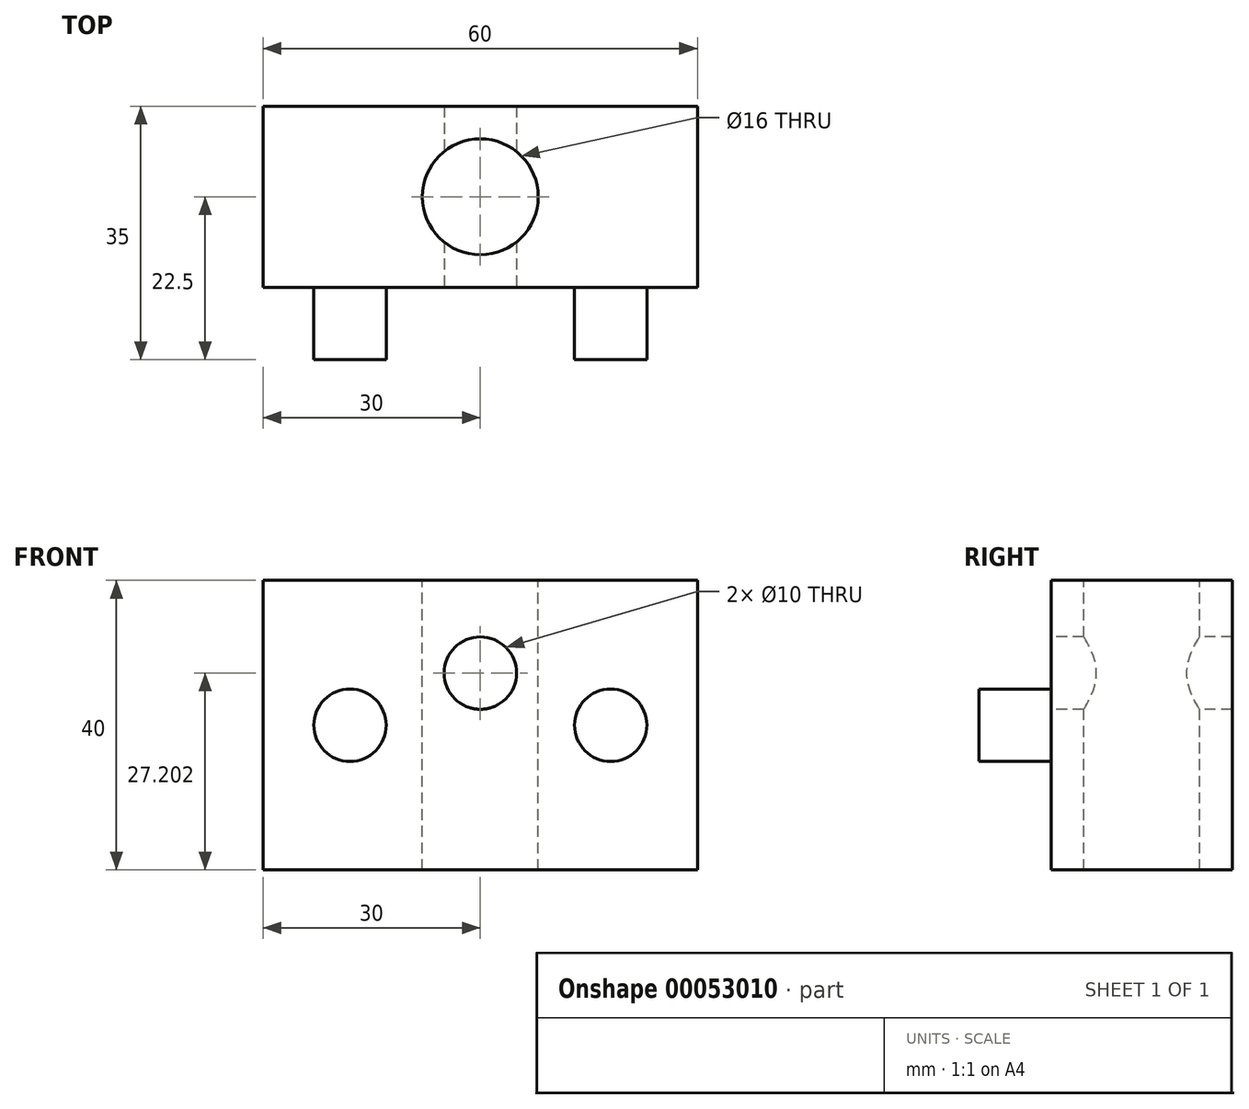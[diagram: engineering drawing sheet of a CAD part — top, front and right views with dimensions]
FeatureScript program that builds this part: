
annotation { "Feature Type Name" : "Feature", "Feature Type Description" : "" }
export const myFeature = defineFeature(function(context is Context, id is Id, definition is map)
    precondition{}
    {
        {
            var Q0;
            Q0=qCreatedBy(makeId("Front.planeOp"),FACE);
            var sketch = newSketch(context, id + "F0", { "sketchPlane" : qUnion([Q0])});
            skLineSegment(sketch, "E0.rect.bottom", {"start": v(30, 20) * mm, "end": v(-30, 20) * mm});
            skLineSegment(sketch, "E0.rect.top", {"start": v(30, -20) * mm, "end": v(-30, -20) * mm});
            skLineSegment(sketch, "E0.rect.left", {"start": v(30, 20) * mm, "end": v(30, -20) * mm});
            skLineSegment(sketch, "E0.rect.right", {"start": v(-30, 20) * mm, "end": v(-30, -20) * mm});
            skPoint(sketch, "E0.rect.middle", {"position": v(0, 0) * mm});
            skSolve(sketch);
        }
        {
            var Q0;
            Q0=makeQuery(id+"F0.imprint","IMPRINT",FACE,{"disambiguationData":[TD([[makeQuery(id+"F0.imprint","IMPRINT",EDGE,{"derivedFrom":sQuery(id+"F0.wireOp",EDGE,"E0.rect.bottom")}),1.0]])]});
            extrude(context, id + "F1", {"entities" : qUnion([Q0]), "endBound" : BoundingType.SYMMETRIC, "depth" : 25 * mm});
        }
        {
            var Q0;
            Q0=makeQuery(id+"F1.opExtrude","SWEPT_FACE",FACE,{"disambiguationData":[OSD([sQuery(id+"F0.wireOp",EDGE,"E0.rect.bottom")])]});
            var sketch = newSketch(context, id + "F2", { "sketchPlane" : qUnion([Q0])});
            skCircle(sketch, "E1", {"center": v(0, 0) * mm, "radius": 8 * mm});
            skSolve(sketch);
        }
        {
            var Q0;
            Q0 = qSketchRegion(id + "F2", true);
            var Q1;
            Q1=makeQuery(id+"F2.imprint","IMPRINT",FACE,{"disambiguationData":[TD([[makeQuery(id+"F2.imprint","IMPRINT",EDGE,{"derivedFrom":sQuery(id+"F2.wireOp",EDGE,"E1")}),1.0]])]});
            extrude(context, id + "F3", {"entities" : qUnion([Q0, Q1]), "operationType" : NewBodyOperationType.REMOVE, "endBound" : BoundingType.THROUGH_ALL, "oppositeDirection" : true, "depth" : 25 * mm});
        }
        {
            var Q0;
            Q0=makeQuery(id+"F1.opExtrude","CAP_FACE",FACE,{"disambiguationData":[OSD([sQuery(id+"F0.wireOp",EDGE,"E0.rect.bottom"),sQuery(id+"F0.wireOp",EDGE,"E0.rect.top"),sQuery(id+"F0.wireOp",EDGE,"E0.rect.left"),sQuery(id+"F0.wireOp",EDGE,"E0.rect.right")])],"isStart":false});
            var sketch = newSketch(context, id + "F4", { "sketchPlane" : qUnion([Q0])});
            skCircle(sketch, "E2", {"center": v(-18, 0) * mm, "radius": 5 * mm});
            skCircle(sketch, "E3", {"center": v(18, 0) * mm, "radius": 5 * mm});
            skSolve(sketch);
        }
        {
            var Q0;
            Q0=makeQuery(id+"F4.imprint","IMPRINT",FACE,{"disambiguationData":[TD([[makeQuery(id+"F4.imprint","IMPRINT",EDGE,{"derivedFrom":sQuery(id+"F4.wireOp",EDGE,"E2")}),1.0]])]});
            var Q1;
            Q1=makeQuery(id+"F4.imprint","IMPRINT",FACE,{"disambiguationData":[TD([[makeQuery(id+"F4.imprint","IMPRINT",EDGE,{"derivedFrom":sQuery(id+"F4.wireOp",EDGE,"E3")}),1.0]])]});
            extrude(context, id + "F5", {"entities" : qUnion([Q0, Q1]), "operationType" : NewBodyOperationType.ADD, "depth" : 10 * mm});
        }
        {
            var Q0;
            Q0=makeQuery(id+"F1.opExtrude","CAP_FACE",FACE,{"disambiguationData":[OSD([sQuery(id+"F0.wireOp",EDGE,"E0.rect.bottom"),sQuery(id+"F0.wireOp",EDGE,"E0.rect.top"),sQuery(id+"F0.wireOp",EDGE,"E0.rect.left"),sQuery(id+"F0.wireOp",EDGE,"E0.rect.right")])],"isStart":false});
            var sketch = newSketch(context, id + "F6", { "sketchPlane" : qUnion([Q0])});
            skCircle(sketch, "E4", {"center": v(0, 7.2) * mm, "radius": 5 * mm});
            skPoint(sketch, "E4.centerSnap0", {"position": v(0, 20) * mm});
            skSolve(sketch);
        }
        {
            var Q0;
            Q0 = qSketchRegion(id + "F6", true);
            extrude(context, id + "F7", {"entities" : qUnion([Q0]), "operationType" : NewBodyOperationType.REMOVE, "oppositeDirection" : true, "depth" : 25 * mm});
        }
    });
